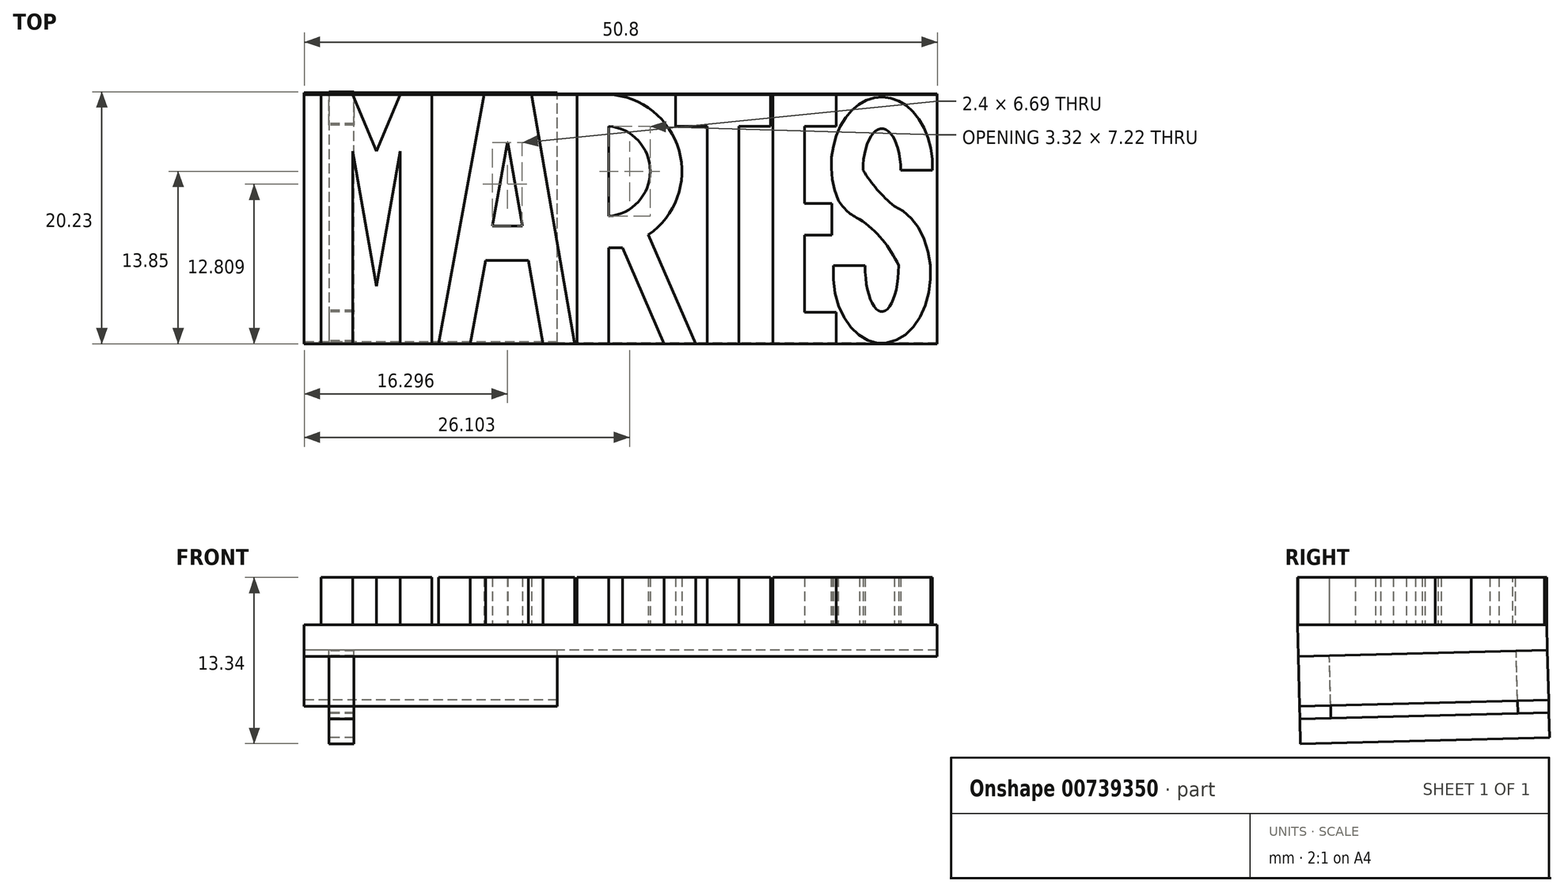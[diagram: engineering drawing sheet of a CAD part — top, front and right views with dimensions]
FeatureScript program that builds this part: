
annotation { "Feature Type Name" : "Feature", "Feature Type Description" : "" }
export const myFeature = defineFeature(function(context is Context, id is Id, definition is map)
    precondition{}
    {
        {
            var Q0;
            Q0=qCreatedBy(makeId("Front.planeOp"),FACE);
            var sketch = newSketch(context, id + "F0", { "sketchPlane" : qUnion([Q0])});
            skArc(sketch, "E0", {"start": v(21, 27.83) * mm, "mid": v(-4.5, 30.73) * mm, "end": v(-30, 27.87) * mm});
            skLineSegment(sketch, "E1", {"start": v(-30, 27.87) * mm, "end": v(-30, 32.87) * mm});
            skLineSegment(sketch, "E2", {"start": v(21, 27.83) * mm, "end": v(21, 32.87) * mm});
            skArc(sketch, "E3", {"start": v(21, 32.87) * mm, "mid": v(-4.5, 35.75) * mm, "end": v(-30, 32.87) * mm});
            skSolve(sketch);
        }
        {
            var Q0;
            Q0=makeQuery(id+"F0.imprint","IMPRINT",FACE,{"disambiguationData":[TD([[makeQuery(id+"F0.imprint","IMPRINT",EDGE,{"derivedFrom":sQuery(id+"F0.wireOp",EDGE,"E0")}),-1.0]])]});
            extrude(context, id + "F1", {"entities" : qUnion([Q0]), "depth" : 20 * mm, "offsetDistance" : 25.4 * mm});
        }
        {
            var Q0;
            Q0=makeQuery(id+"F1.opExtrude","SWEPT_FACE",FACE,{"disambiguationData":[OSD([sQuery(id+"F0.wireOp",EDGE,"E1")])]});
            var sketch = newSketch(context, id + "F2", { "sketchPlane" : qUnion([Q0])});
            skLineSegment(sketch, "E4", {"start": v(20, 32.87) * mm, "end": v(19.94, 30.33) * mm});
            skLineSegment(sketch, "E5", {"start": v(19.94, 30.33) * mm, "end": v(-0.05, 30.84) * mm});
            skLineSegment(sketch, "E6", {"start": v(-0.05, 30.84) * mm, "end": v(0, 32.87) * mm});
            skLineSegment(sketch, "E7", {"start": v(0, 32.87) * mm, "end": v(20, 32.87) * mm});
            skSolve(sketch);
        }
        {
            var Q0;
            Q0=qSketchRegion(id+"F2",true);
            extrude(context, id + "F3", {"entities" : qUnion([Q0]), "oppositeDirection" : true, "depth" : 50.8 * mm, "offsetDistance" : 25.4 * mm});
        }
        {
            var Q0;
            Q0=makeQuery(id+"F3.opExtrude","SWEPT_FACE",FACE,{"disambiguationData":[OSD([sQuery(id+"F2.wireOp",EDGE,"E5")])]});
            var sketch = newSketch(context, id + "F4", { "sketchPlane" : qUnion([Q0])});
            skLineSegment(sketch, "E8", {"start": v(-28, 19.17) * mm, "end": v(-26, 19.17) * mm});
            skLineSegment(sketch, "E9", {"start": v(-26, 19.17) * mm, "end": v(-26, 16.67) * mm});
            skLineSegment(sketch, "E10", {"start": v(-26, 16.67) * mm, "end": v(-28, 16.67) * mm});
            skLineSegment(sketch, "E11", {"start": v(-28, 16.67) * mm, "end": v(-28, 19.17) * mm});
            skLineSegment(sketch, "E12", {"start": v(-28, 1.67) * mm, "end": v(-28, -0.83) * mm});
            skLineSegment(sketch, "E13", {"start": v(-28, -0.83) * mm, "end": v(-26, -0.83) * mm});
            skLineSegment(sketch, "E14", {"start": v(-26, -0.83) * mm, "end": v(-26, 1.67) * mm});
            skLineSegment(sketch, "E15", {"start": v(-26, 1.67) * mm, "end": v(-28, 1.67) * mm});
            skLineSegment(sketch, "E16", {"start": v(-26, 1.67) * mm, "end": v(-26, 16.67) * mm});
            skLineSegment(sketch, "E17", {"start": v(-28, 1.67) * mm, "end": v(-28, 16.67) * mm});
            skSolve(sketch);
        }
        {
            var Q0;
            Q0=makeQuery(id+"F4.imprint","IMPRINT",FACE,{"disambiguationData":[TD([[makeQuery(id+"F4.imprint","IMPRINT",EDGE,{"derivedFrom":sQuery(id+"F4.wireOp",EDGE,"E8")}),1.0]])]});
            var Q1;
            Q1=makeQuery(id+"F4.imprint","IMPRINT",FACE,{"disambiguationData":[TD([[makeQuery(id+"F4.imprint","IMPRINT",EDGE,{"derivedFrom":sQuery(id+"F4.wireOp",EDGE,"E12")}),1.0]])]});
            extrude(context, id + "F5", {"entities" : qUnion([Q0, Q1]), "depth" : 5 * mm, "offsetDistance" : 25.4 * mm});
        }
        {
            var Q0;
            Q0=makeQuery(id+"F5.opExtrude","CAP_FACE",FACE,{"disambiguationData":[OSD([sQuery(id+"F4.wireOp",EDGE,"E8"),sQuery(id+"F4.wireOp",EDGE,"E9"),sQuery(id+"F4.wireOp",EDGE,"E10"),sQuery(id+"F4.wireOp",EDGE,"E11")])],"isStart":false});
            var sketch = newSketch(context, id + "F6", { "sketchPlane" : qUnion([Q0])});
            skLineSegment(sketch, "E18", {"start": v(-26, 19.17) * mm, "end": v(-26, -0.83) * mm});
            skLineSegment(sketch, "E19", {"start": v(-26, -0.83) * mm, "end": v(-28, -0.83) * mm});
            skLineSegment(sketch, "E20", {"start": v(-28, -0.83) * mm, "end": v(-28, 19.17) * mm});
            skLineSegment(sketch, "E21", {"start": v(-28, 19.17) * mm, "end": v(-26, 19.17) * mm});
            skSolve(sketch);
        }
        {
            var Q0;
            {var subQ2=sQuery(id+"F6.wireOp",EDGE,"E19");Q0=makeQuery(id+"F6.imprint","IMPRINT",FACE,{"disambiguationData":[TD([[makeQuery(id+"F6.imprint","IMPRINT",EDGE,{"derivedFrom":subQ2}),-1.0]])]});}
            var Q1;
            {var subQ0=sQuery(id+"F6.wireOp",EDGE,"E21");Q1=makeQuery(id+"F6.imprint","IMPRINT",FACE,{"disambiguationData":[TD([[makeQuery(id+"F6.imprint","IMPRINT",EDGE,{"derivedFrom":subQ0}),1.0]])]});}
            extrude(context, id + "F7", {"entities" : qUnion([Q0, Q1]), "depth" : 2 * mm, "offsetDistance" : 25.4 * mm});
        }
        {
            var Q0;
            Q0=makeQuery(id+"F3.opExtrude","SWEPT_FACE",FACE,{"disambiguationData":[OSD([sQuery(id+"F2.wireOp",EDGE,"E7")])]});
            var sketch = newSketch(context, id + "F8", { "sketchPlane" : qUnion([Q0])});
            skLineSegment(sketch, "E22", {"start": v(-28.65, 0) * mm, "end": v(-28.65, -20) * mm});
            skLineSegment(sketch, "E23", {"start": v(-28.65, -20) * mm, "end": v(-26.11, -20) * mm});
            skLineSegment(sketch, "E24", {"start": v(-26.11, -20) * mm, "end": v(-26.11, -4.55) * mm});
            skLineSegment(sketch, "E25", {"start": v(-26.11, -4.55) * mm, "end": v(-24.2, -15.36) * mm});
            skLineSegment(sketch, "E26", {"start": v(-24.2, -15.36) * mm, "end": v(-22.3, -4.55) * mm});
            skLineSegment(sketch, "E27", {"start": v(-22.3, -4.55) * mm, "end": v(-22.3, -20) * mm});
            skLineSegment(sketch, "E28", {"start": v(-22.3, -20) * mm, "end": v(-19.76, -20) * mm});
            skLineSegment(sketch, "E29", {"start": v(-19.76, -20) * mm, "end": v(-19.76, 0) * mm});
            skLineSegment(sketch, "E30", {"start": v(-19.76, 0) * mm, "end": v(-22.3, 0) * mm});
            skLineSegment(sketch, "E31", {"start": v(-22.3, 0) * mm, "end": v(-24.2, -4.55) * mm});
            skLineSegment(sketch, "E32", {"start": v(-24.2, -4.55) * mm, "end": v(-26.11, 0) * mm});
            skLineSegment(sketch, "E33", {"start": v(-26.11, 0) * mm, "end": v(-28.65, 0) * mm});
            skSolve(sketch);
        }
        {
            var Q0;
            Q0=makeQuery(id+"F8.imprint","IMPRINT",FACE,{"disambiguationData":[TD([[makeQuery(id+"F8.imprint","IMPRINT",EDGE,{"derivedFrom":sQuery(id+"F8.wireOp",EDGE,"E22")}),1.0]])]});
            extrude(context, id + "F9", {"entities" : qUnion([Q0]), "depth" : 3.8 * mm, "offsetDistance" : 25.4 * mm});
        }
        {
            var Q0;
            {var subQ1=sQuery(id+"F2.wireOp",EDGE,"E7");Q0=makeQuery(id+"F9.boolean.opBoolean","SPLIT",FACE,{"disambiguationData":[TD([makeQuery(id+"F9.opExtrude","SWEPT_FACE",FACE,{"disambiguationData":[OSD([sQuery(id+"F8.wireOp",EDGE,"E29")])]})])],"derivedFrom":makeQuery(id+"F3.opExtrude","SWEPT_FACE",FACE,{"disambiguationData":[OSD([subQ1])]})});}
            var sketch = newSketch(context, id + "F10", { "sketchPlane" : qUnion([Q0])});
            skLineSegment(sketch, "E34", {"start": v(-4.77, 0) * mm, "end": v(-4.77, -20) * mm});
            skLineSegment(sketch, "E35", {"start": v(-4.77, -20) * mm, "end": v(-2.74, -20) * mm});
            skLineSegment(sketch, "E36", {"start": v(-2.74, -20) * mm, "end": v(-2.74, 0) * mm});
            skLineSegment(sketch, "E37", {"start": v(-2.74, 0) * mm, "end": v(-4.77, 0) * mm});
            skSolve(sketch);
        }
        {
            var Q0;
            Q0=makeQuery(id+"F10.imprint","IMPRINT",FACE,{"disambiguationData":[TD([[makeQuery(id+"F10.imprint","IMPRINT",EDGE,{"derivedFrom":sQuery(id+"F10.wireOp",EDGE,"E34")}),1.0]])]});
            extrude(context, id + "F11", {"entities" : qUnion([Q0]), "depth" : 3.8 * mm, "offsetDistance" : 25.4 * mm});
        }
        {
            var Q0;
            Q0=makeQuery(id+"F3.opExtrude","SWEPT_FACE",FACE,{"disambiguationData":[OSD([sQuery(id+"F2.wireOp",EDGE,"E7")])]});
            var sketch = newSketch(context, id + "F12", { "sketchPlane" : qUnion([Q0])});
            skLineSegment(sketch, "E38", {"start": v(-1.78, 0) * mm, "end": v(0.26, 0) * mm});
            skLineSegment(sketch, "E39", {"start": v(-1.78, -20) * mm, "end": v(0.26, -20) * mm});
            skLineSegment(sketch, "E40", {"start": v(-1.78, 0) * mm, "end": v(-1.78, -20) * mm});
            skLineSegment(sketch, "E41", {"start": v(3.05, -20) * mm, "end": v(5.08, -20) * mm});
            skLineSegment(sketch, "E42", {"start": v(3.05, 0) * mm, "end": v(5.08, 0) * mm});
            skLineSegment(sketch, "E43", {"start": v(5.08, 0) * mm, "end": v(5.08, -20) * mm});
            skLineSegment(sketch, "E44", {"start": v(0.26, -20) * mm, "end": v(0.26, -8.96) * mm});
            skLineSegment(sketch, "E45", {"start": v(0.26, -8.96) * mm, "end": v(3.05, -20) * mm});
            skLineSegment(sketch, "E46", {"start": v(3.05, 0) * mm, "end": v(3.05, -10.13) * mm});
            skLineSegment(sketch, "E47", {"start": v(3.05, -10.13) * mm, "end": v(0.26, 0) * mm});
            skSolve(sketch);
        }
        {
            var Q0;
            Q0=makeQuery(id+"F12.imprint","IMPRINT",FACE,{"disambiguationData":[TD([[makeQuery(id+"F12.imprint","IMPRINT",EDGE,{"derivedFrom":sQuery(id+"F12.wireOp",EDGE,"E38")}),1.0]])]});
            extrude(context, id + "F13", {"entities" : qUnion([Q0]), "depth" : 3.8 * mm, "offsetDistance" : 25.4 * mm});
        }
        {
            var Q0;
            {var subQ1=sQuery(id+"F2.wireOp",EDGE,"E7");Q0=makeQuery(id+"F13.boolean.opBoolean","SPLIT",FACE,{"disambiguationData":[TD([makeQuery(id+"F13.opExtrude","SWEPT_FACE",FACE,{"disambiguationData":[OSD([sQuery(id+"F12.wireOp",EDGE,"E43")])]})])],"derivedFrom":makeQuery(id+"F3.opExtrude","SWEPT_FACE",FACE,{"disambiguationData":[OSD([subQ1])]})});}
            var sketch = newSketch(context, id + "F14", { "sketchPlane" : qUnion([Q0])});
            skEllipse(sketch, "E48", {"center": v(8.95, -10.06) * mm, "majorRadius": 10 * mm, "minorRadius": 3.81 * mm, "majorAxis": v(0, 1)});
            skEllipse(sketch, "E49", {"center": v(8.95, -10.06) * mm, "majorRadius": 7.97 * mm, "minorRadius": 1.78 * mm, "majorAxis": v(0, 1)});
            skLineSegment(sketch, "E50", {"start": v(10.73, -10.06) * mm, "end": v(12.76, -10.06) * mm});
            skLineSegment(sketch, "E51", {"start": v(8.95, -0.06) * mm, "end": v(8.95, -2.1) * mm});
            skLineSegment(sketch, "E52", {"start": v(8.95, -10.06) * mm, "end": v(10.73, -10.06) * mm});
            skLineSegment(sketch, "E53", {"start": v(8.95, -10.06) * mm, "end": v(8.95, -12.1) * mm});
            skLineSegment(sketch, "E54", {"start": v(8.95, -12.1) * mm, "end": v(10.67, -12.1) * mm});
            skLineSegment(sketch, "E55", {"start": v(12.54, -6.74) * mm, "end": v(10.56, -6.74) * mm});
            skLineSegment(sketch, "E56", {"start": v(8.95, -0.06) * mm, "end": v(8.95, -20.06) * mm});
            skSolve(sketch);
        }
        {
            var Q0;
            {var subQ0=sQuery(id+"F14.wireOp",EDGE,"E51");Q0=makeQuery(id+"F14.imprint","IMPRINT",FACE,{"disambiguationData":[TD([[makeQuery(id+"F14.imprint","IMPRINT",EDGE,{"derivedFrom":subQ0}),1.0]])]});}
            var Q1;
            {var subQ0=sQuery(id+"F14.wireOp",EDGE,"E50");Q1=makeQuery(id+"F14.imprint","IMPRINT",FACE,{"disambiguationData":[TD([[makeQuery(id+"F14.imprint","IMPRINT",EDGE,{"derivedFrom":subQ0}),-1.0]])]});}
            var Q2;
            {var subQ0=sQuery(id+"F14.wireOp",EDGE,"E52");Q2=makeQuery(id+"F14.imprint","IMPRINT",FACE,{"disambiguationData":[TD([[makeQuery(id+"F14.imprint","IMPRINT",EDGE,{"derivedFrom":subQ0}),-1.0]])]});}
            var Q3;
            {var subQ0=sQuery(id+"F14.wireOp",EDGE,"E56");var subQ3=sQuery(id+"F14.wireOp",EDGE,"E49");var subQ4=makeQuery(id+"F14.imprint","INTERSECT",VERTEX,{"disambiguationData":[OD(0.0)],"derivedFrom":[subQ3,subQ0]});Q3=makeQuery(id+"F14.imprint","IMPRINT",FACE,{"disambiguationData":[TD([[makeQuery(id+"F14.imprint","IMPRINT",EDGE,{"disambiguationData":[TD([[subQ4,1.0]])],"derivedFrom":subQ3}),-1.0]])]});}
            var Q4;
            {var subQ7=sQuery(id+"F14.wireOp",EDGE,"E55");Q4=makeQuery(id+"F14.imprint","IMPRINT",FACE,{"disambiguationData":[TD([[makeQuery(id+"F14.imprint","IMPRINT",EDGE,{"derivedFrom":subQ7}),-1.0]])]});}
            extrude(context, id + "F15", {"entities" : qUnion([Q0, Q1, Q2, Q3, Q4]), "depth" : 3.8 * mm, "offsetDistance" : 25.4 * mm});
        }
        {
            var Q0;
            Q0=makeQuery(id+"F3.opExtrude","SWEPT_FACE",FACE,{"disambiguationData":[OSD([sQuery(id+"F2.wireOp",EDGE,"E7")])]});
            var sketch = newSketch(context, id + "F16", { "sketchPlane" : qUnion([Q0])});
            skEllipse(sketch, "E57", {"center": v(16.77, -10) * mm, "majorRadius": 10 * mm, "minorRadius": 3.95 * mm, "majorAxis": v(0, 1)});
            skPoint(sketch, "E57.centerSnap0", {"position": v(20.8, -10) * mm});
            skEllipse(sketch, "E58", {"center": v(16.77, -10) * mm, "majorRadius": 7.5 * mm, "minorRadius": 2.22 * mm, "majorAxis": v(0, 1)});
            skSolve(sketch);
        }
        {
            var Q0;
            Q0=makeQuery(id+"F16.imprint","IMPRINT",FACE,{"disambiguationData":[TD([[makeQuery(id+"F16.imprint","IMPRINT",EDGE,{"derivedFrom":sQuery(id+"F16.wireOp",EDGE,"E58")}),-1.0]])]});
            extrude(context, id + "F17", {"entities" : qUnion([Q0]), "depth" : 3.8 * mm, "offsetDistance" : 25.4 * mm});
        }
        {
            var Q0;
            Q0=makeQuery(id+"F1.opExtrude","SWEPT_BODY",BODY,{"disambiguationData":[OSD([sQuery(id+"F0.wireOp",EDGE,"E0"),sQuery(id+"F0.wireOp",EDGE,"E1"),sQuery(id+"F0.wireOp",EDGE,"E2"),sQuery(id+"F0.wireOp",EDGE,"E3")])]});
            deleteBodies(context, id + "F18", {"entities" : qUnion([Q0])});
        }
        {
            var Q0;
            Q0=makeQuery(id+"F11.opExtrude","SWEPT_BODY",BODY,{"disambiguationData":[OSD([sQuery(id+"F10.wireOp",EDGE,"E34"),sQuery(id+"F10.wireOp",EDGE,"E35"),sQuery(id+"F10.wireOp",EDGE,"E36"),sQuery(id+"F10.wireOp",EDGE,"E37")])]});
            deleteBodies(context, id + "F19", {"entities" : qUnion([Q0])});
        }
        {
            var Q0;
            Q0=makeQuery(id+"F13.opExtrude","SWEPT_BODY",BODY,{"disambiguationData":[OSD([sQuery(id+"F12.wireOp",EDGE,"E38"),sQuery(id+"F12.wireOp",EDGE,"E39"),sQuery(id+"F12.wireOp",EDGE,"E40"),sQuery(id+"F12.wireOp",EDGE,"E41"),sQuery(id+"F12.wireOp",EDGE,"E42"),sQuery(id+"F12.wireOp",EDGE,"E43"),sQuery(id+"F12.wireOp",EDGE,"E44"),sQuery(id+"F12.wireOp",EDGE,"E45"),sQuery(id+"F12.wireOp",EDGE,"E46"),sQuery(id+"F12.wireOp",EDGE,"E47")])]});
            deleteBodies(context, id + "F20", {"entities" : qUnion([Q0])});
        }
        {
            var Q0;
            Q0=makeQuery(id+"F15.opExtrude","SWEPT_BODY",BODY,{"disambiguationData":[OSD([sQuery(id+"F0.wireOp",EDGE,"E1"),sQuery(id+"F2.wireOp",EDGE,"E4"),sQuery(id+"F2.wireOp",EDGE,"E7"),sQuery(id+"F14.wireOp",EDGE,"E48"),sQuery(id+"F14.wireOp",EDGE,"E49"),sQuery(id+"F14.wireOp",EDGE,"E50"),sQuery(id+"F14.wireOp",EDGE,"E52"),sQuery(id+"F14.wireOp",EDGE,"E54"),sQuery(id+"F14.wireOp",EDGE,"E55"),sQuery(id+"F14.wireOp",EDGE,"E56")])]});
            deleteBodies(context, id + "F21", {"entities" : qUnion([Q0])});
        }
        {
            var Q0;
            Q0=makeQuery(id+"F17.opExtrude","SWEPT_BODY",BODY,{"disambiguationData":[OSD([sQuery(id+"F16.wireOp",EDGE,"E57"),sQuery(id+"F16.wireOp",EDGE,"E58")])]});
            deleteBodies(context, id + "F22", {"entities" : qUnion([Q0])});
        }
        {
            var Q0;
            Q0=makeQuery(id+"F3.opExtrude","SWEPT_FACE",FACE,{"disambiguationData":[OSD([sQuery(id+"F2.wireOp",EDGE,"E7")])]});
            var sketch = newSketch(context, id + "F23", { "sketchPlane" : qUnion([Q0])});
            skLineSegment(sketch, "E59", {"start": v(-19.21, -20) * mm, "end": v(-16.67, -20) * mm});
            skLineSegment(sketch, "E60", {"start": v(-10.83, -20) * mm, "end": v(-8.29, -20) * mm});
            skLineSegment(sketch, "E61", {"start": v(-16.67, -20) * mm, "end": v(-15.43, -13.32) * mm});
            skLineSegment(sketch, "E62", {"start": v(-15.43, -13.32) * mm, "end": v(-12, -13.32) * mm});
            skLineSegment(sketch, "E63", {"start": v(-12, -13.32) * mm, "end": v(-10.83, -20) * mm});
            skLineSegment(sketch, "E64", {"start": v(-19.21, -20) * mm, "end": v(-15.56, 0) * mm});
            skLineSegment(sketch, "E65", {"start": v(-15.56, 0) * mm, "end": v(-11.75, 0) * mm});
            skLineSegment(sketch, "E66", {"start": v(-11.75, 0) * mm, "end": v(-8.29, -20) * mm});
            skLineSegment(sketch, "E67", {"start": v(-14.9, -10.54) * mm, "end": v(-12.5, -10.54) * mm});
            skLineSegment(sketch, "E68", {"start": v(-12.5, -10.54) * mm, "end": v(-13.66, -3.85) * mm});
            skLineSegment(sketch, "E69", {"start": v(-13.66, -3.85) * mm, "end": v(-13.68, -3.85) * mm});
            skLineSegment(sketch, "E70", {"start": v(-13.68, -3.85) * mm, "end": v(-14.9, -10.54) * mm});
            skSolve(sketch);
        }
        {
            var Q0;
            Q0=makeQuery(id+"F23.imprint","IMPRINT",FACE,{"disambiguationData":[TD([[makeQuery(id+"F23.imprint","IMPRINT",EDGE,{"derivedFrom":sQuery(id+"F23.wireOp",EDGE,"E59")}),-1.0]])]});
            extrude(context, id + "F24", {"entities" : qUnion([Q0]), "depth" : 3.8 * mm, "offsetDistance" : 25.4 * mm});
        }
        {
            var Q0;
            Q0=makeQuery(id+"F3.opExtrude","SWEPT_FACE",FACE,{"disambiguationData":[OSD([sQuery(id+"F2.wireOp",EDGE,"E7")])]});
            var sketch = newSketch(context, id + "F25", { "sketchPlane" : qUnion([Q0])});
            skLineSegment(sketch, "E71", {"start": v(-8.1, 0) * mm, "end": v(-8.1, -20) * mm});
            skLineSegment(sketch, "E72", {"start": v(-8.1, -20) * mm, "end": v(-5.56, -20) * mm});
            skLineSegment(sketch, "E73", {"start": v(-5.56, -20) * mm, "end": v(-5.56, -12.3) * mm});
            skLineSegment(sketch, "E74", {"start": v(-8.1, 0) * mm, "end": v(-5.56, 0) * mm});
            skArc(sketch, "E75", {"start": v(-2.39, -11.25) * mm, "mid": v(0.07, -4.48) * mm, "end": v(-5.56, 0) * mm});
            skLineSegment(sketch, "E76", {"start": v(-5.56, -12.3) * mm, "end": v(-4.47, -12.3) * mm});
            skLineSegment(sketch, "E77", {"start": v(-4.47, -12.3) * mm, "end": v(-1.13, -20) * mm});
            skLineSegment(sketch, "E78", {"start": v(-1.13, -20) * mm, "end": v(1.4, -20) * mm});
            skLineSegment(sketch, "E79", {"start": v(1.4, -20) * mm, "end": v(-2.39, -11.25) * mm});
            skLineSegment(sketch, "E80", {"start": v(-5.56, -2.54) * mm, "end": v(-5.56, -9.76) * mm});
            skArc(sketch, "E81", {"start": v(-5.56, -9.76) * mm, "mid": v(-2.24, -6.15) * mm, "end": v(-5.56, -2.54) * mm});
            skLineSegment(sketch, "E82", {"start": v(-2.24, -6.15) * mm, "end": v(0.3, -6.15) * mm});
            skSolve(sketch);
        }
        {
            var Q0;
            Q0 = qSketchRegion(id + "F25", true);
            extrude(context, id + "F26", {"entities" : qUnion([Q0]), "depth" : 3.8 * mm, "offsetDistance" : 25.4 * mm});
        }
        {
            var Q0;
            Q0=makeQuery(id+"F3.opExtrude","SWEPT_FACE",FACE,{"disambiguationData":[OSD([sQuery(id+"F2.wireOp",EDGE,"E7")])]});
            var sketch = newSketch(context, id + "F27", { "sketchPlane" : qUnion([Q0])});
            skLineSegment(sketch, "E83", {"start": v(-0.2, 0) * mm, "end": v(-0.2, -2.54) * mm});
            skLineSegment(sketch, "E84", {"start": v(-0.2, -2.54) * mm, "end": v(2.35, -2.54) * mm});
            skLineSegment(sketch, "E85", {"start": v(2.35, -2.54) * mm, "end": v(2.35, -20) * mm});
            skLineSegment(sketch, "E86", {"start": v(2.35, -20) * mm, "end": v(4.89, -20) * mm});
            skLineSegment(sketch, "E87", {"start": v(4.89, -20) * mm, "end": v(4.89, -2.54) * mm});
            skLineSegment(sketch, "E88", {"start": v(4.89, -2.54) * mm, "end": v(7.43, -2.54) * mm});
            skLineSegment(sketch, "E89", {"start": v(7.43, -2.54) * mm, "end": v(7.43, 0) * mm});
            skLineSegment(sketch, "E90", {"start": v(7.43, 0) * mm, "end": v(-0.2, 0) * mm});
            skSolve(sketch);
        }
        {
            var Q0;
            Q0 = qSketchRegion(id + "F27", true);
            extrude(context, id + "F28", {"entities" : qUnion([Q0]), "depth" : 3.8 * mm, "offsetDistance" : 25.4 * mm});
        }
        {
            var Q0;
            Q0=makeQuery(id+"F3.opExtrude","SWEPT_FACE",FACE,{"disambiguationData":[OSD([sQuery(id+"F2.wireOp",EDGE,"E7")])]});
            var sketch = newSketch(context, id + "F29", { "sketchPlane" : qUnion([Q0])});
            skLineSegment(sketch, "E91", {"start": v(7.62, 0) * mm, "end": v(7.62, -20) * mm});
            skLineSegment(sketch, "E92", {"start": v(7.62, -20) * mm, "end": v(12.7, -20) * mm});
            skLineSegment(sketch, "E93", {"start": v(12.7, -20) * mm, "end": v(12.7, -17.46) * mm});
            skLineSegment(sketch, "E94", {"start": v(12.7, -17.46) * mm, "end": v(10.16, -17.46) * mm});
            skLineSegment(sketch, "E95", {"start": v(10.16, -17.46) * mm, "end": v(10.16, -11.27) * mm});
            skLineSegment(sketch, "E96", {"start": v(10.16, -11.27) * mm, "end": v(12.35, -11.27) * mm});
            skLineSegment(sketch, "E97", {"start": v(12.35, -11.27) * mm, "end": v(12.35, -8.73) * mm});
            skLineSegment(sketch, "E98", {"start": v(12.35, -8.73) * mm, "end": v(10.16, -8.73) * mm});
            skLineSegment(sketch, "E99", {"start": v(10.16, -8.73) * mm, "end": v(10.16, -2.54) * mm});
            skLineSegment(sketch, "E100", {"start": v(10.16, -2.54) * mm, "end": v(12.7, -2.54) * mm});
            skLineSegment(sketch, "E101", {"start": v(12.7, -2.54) * mm, "end": v(12.7, 0) * mm});
            skLineSegment(sketch, "E102", {"start": v(12.7, 0) * mm, "end": v(7.62, 0) * mm});
            skSolve(sketch);
        }
        {
            var Q0;
            Q0 = qSketchRegion(id + "F29", true);
            extrude(context, id + "F30", {"entities" : qUnion([Q0]), "depth" : 3.8 * mm, "offsetDistance" : 25.4 * mm});
        }
        {
            var Q0;
            Q0=makeQuery(id+"F3.opExtrude","SWEPT_FACE",FACE,{"disambiguationData":[OSD([sQuery(id+"F2.wireOp",EDGE,"E7")])]});
            var sketch = newSketch(context, id + "F31", { "sketchPlane" : qUnion([Q0])});
            skEllipse(sketch, "E103", {"center": v(16.35, -5.7) * mm, "majorRadius": 5.5 * mm, "minorRadius": 4.06 * mm, "majorAxis": v(0, -1)});
            skEllipse(sketch, "E104", {"center": v(16.35, -6.07) * mm, "majorRadius": 3.34 * mm, "minorRadius": 1.51 * mm, "majorAxis": v(0, 1)});
            skLineSegment(sketch, "E105", {"start": v(16.35, -0.2) * mm, "end": v(16.35, -2.73) * mm});
            skLineSegment(sketch, "E106", {"start": v(14.84, -6.07) * mm, "end": v(12.3, -6.07) * mm});
            skLineSegment(sketch, "E107", {"start": v(17.86, -6.07) * mm, "end": v(20.4, -6.07) * mm});
            skEllipse(sketch, "E108", {"center": v(16.35, -14.37) * mm, "majorRadius": 5.59 * mm, "minorRadius": 3.91 * mm, "majorAxis": v(0, 1)});
            skEllipse(sketch, "E109", {"center": v(16.35, -13.73) * mm, "majorRadius": 3.68 * mm, "minorRadius": 1.35 * mm, "majorAxis": v(0, -1)});
            skLineSegment(sketch, "E110", {"start": v(16.35, -17.42) * mm, "end": v(16.35, -19.96) * mm});
            skLineSegment(sketch, "E111", {"start": v(15, -13.73) * mm, "end": v(12.46, -13.73) * mm});
            skLineSegment(sketch, "E112", {"start": v(17.7, -13.73) * mm, "end": v(20.24, -13.73) * mm});
            skArc(sketch, "E113", {"start": v(14.84, -6.07) * mm, "mid": v(16.58, -8.27) * mm, "end": v(18.8, -10) * mm});
            skPoint(sketch, "E113.endSnap0", {"position": v(20.8, -10) * mm});
            skArc(sketch, "E114", {"start": v(20.24, -13.73) * mm, "mid": v(19.99, -11.68) * mm, "end": v(18.8, -10) * mm});
            skArc(sketch, "E115", {"start": v(12.3, -6.07) * mm, "mid": v(12.8, -8.4) * mm, "end": v(14.56, -10) * mm});
            skArc(sketch, "E116", {"start": v(17.7, -13.73) * mm, "mid": v(16.4, -11.65) * mm, "end": v(14.56, -10) * mm});
            skLineSegment(sketch, "E117", {"start": v(15.55, -10.77) * mm, "end": v(17.2, -8.84) * mm});
            skSolve(sketch);
        }
        {
            var Q0;
            {var subQ0=sQuery(id+"F31.wireOp",EDGE,"E105");Q0=makeQuery(id+"F31.imprint","IMPRINT",FACE,{"disambiguationData":[TD([[makeQuery(id+"F31.imprint","IMPRINT",EDGE,{"derivedFrom":subQ0}),1.0]])]});}
            var Q1;
            {var subQ0=sQuery(id+"F31.wireOp",EDGE,"E105");Q1=makeQuery(id+"F31.imprint","IMPRINT",FACE,{"disambiguationData":[TD([[makeQuery(id+"F31.imprint","IMPRINT",EDGE,{"derivedFrom":subQ0}),-1.0]])]});}
            var Q2;
            {var subQ0=sQuery(id+"F31.wireOp",EDGE,"E106");Q2=makeQuery(id+"F31.imprint","IMPRINT",FACE,{"disambiguationData":[TD([[makeQuery(id+"F31.imprint","IMPRINT",EDGE,{"derivedFrom":subQ0}),1.0]])]});}
            var Q3;
            {var subQ5=sQuery(id+"F31.wireOp",EDGE,"E112");Q3=makeQuery(id+"F31.imprint","IMPRINT",FACE,{"disambiguationData":[TD([[makeQuery(id+"F31.imprint","IMPRINT",EDGE,{"derivedFrom":subQ5}),1.0]])]});}
            var Q4;
            {var subQ0=sQuery(id+"F31.wireOp",EDGE,"E110");Q4=makeQuery(id+"F31.imprint","IMPRINT",FACE,{"disambiguationData":[TD([[makeQuery(id+"F31.imprint","IMPRINT",EDGE,{"derivedFrom":subQ0}),1.0]])]});}
            var Q5;
            {var subQ0=sQuery(id+"F31.wireOp",EDGE,"E110");Q5=makeQuery(id+"F31.imprint","IMPRINT",FACE,{"disambiguationData":[TD([[makeQuery(id+"F31.imprint","IMPRINT",EDGE,{"derivedFrom":subQ0}),-1.0]])]});}
            var Q6;
            {var subQ0=sQuery(id+"F31.wireOp",EDGE,"E109");var subQ1=sQuery(id+"F31.wireOp",EDGE,"E103");var subQ2=makeQuery(id+"F31.imprint","INTERSECT",VERTEX,{"disambiguationData":[OD(0.0)],"derivedFrom":[subQ1,subQ0]});Q6=makeQuery(id+"F31.imprint","IMPRINT",FACE,{"disambiguationData":[TD([[makeQuery(id+"F31.imprint","IMPRINT",EDGE,{"disambiguationData":[TD([[subQ2,1.0]])],"derivedFrom":subQ1}),1.0]])]});}
            var Q7;
            {var subQ0=sQuery(id+"F31.wireOp",EDGE,"E109");var subQ1=sQuery(id+"F31.wireOp",EDGE,"E103");var subQ2=makeQuery(id+"F31.imprint","INTERSECT",VERTEX,{"disambiguationData":[OD(0.0)],"derivedFrom":[subQ1,subQ0]});Q7=makeQuery(id+"F31.imprint","IMPRINT",FACE,{"disambiguationData":[TD([[makeQuery(id+"F31.imprint","IMPRINT",EDGE,{"disambiguationData":[TD([[subQ2,1.0]])],"derivedFrom":subQ1}),-1.0]])]});}
            var Q8;
            {var subQ1=sQuery(id+"F31.wireOp",EDGE,"E104");var subQ3=sQuery(id+"F31.wireOp",EDGE,"E108");var subQ4=makeQuery(id+"F31.imprint","INTERSECT",VERTEX,{"disambiguationData":[OD(0.0)],"derivedFrom":[subQ1,subQ3]});Q8=makeQuery(id+"F31.imprint","IMPRINT",FACE,{"disambiguationData":[TD([[makeQuery(id+"F31.imprint","IMPRINT",EDGE,{"disambiguationData":[TD([[subQ4,1.0]])],"derivedFrom":subQ3}),-1.0]])]});}
            var Q9;
            {var subQ0=sQuery(id+"F31.wireOp",EDGE,"E108");var subQ1=sQuery(id+"F31.wireOp",EDGE,"E104");var subQ2=makeQuery(id+"F31.imprint","INTERSECT",VERTEX,{"disambiguationData":[OD(0.0)],"derivedFrom":[subQ1,subQ0]});Q9=makeQuery(id+"F31.imprint","IMPRINT",FACE,{"disambiguationData":[TD([[makeQuery(id+"F31.imprint","IMPRINT",EDGE,{"disambiguationData":[TD([[subQ2,-1.0]])],"derivedFrom":subQ1}),1.0]])]});}
            var Q10;
            {var subQ3=sQuery(id+"F31.wireOp",EDGE,"E108");var subQ9=sQuery(id+"F31.wireOp",EDGE,"E104");var subQ10=makeQuery(id+"F31.imprint","INTERSECT",VERTEX,{"disambiguationData":[OD(0.0)],"derivedFrom":[subQ9,subQ3]});Q10=makeQuery(id+"F31.imprint","IMPRINT",FACE,{"disambiguationData":[TD([[makeQuery(id+"F31.imprint","IMPRINT",EDGE,{"disambiguationData":[TD([[subQ10,-1.0]])],"derivedFrom":subQ9}),-1.0]])]});}
            var Q11;
            {var subQ0=sQuery(id+"F31.wireOp",EDGE,"E117");var subQ1=sQuery(id+"F31.wireOp",EDGE,"E109");var subQ3=makeQuery(id+"F31.imprint","INTERSECT",VERTEX,{"derivedFrom":[subQ1,subQ0]});Q11=makeQuery(id+"F31.imprint","IMPRINT",FACE,{"disambiguationData":[TD([[makeQuery(id+"F31.imprint","IMPRINT",EDGE,{"disambiguationData":[TD([[subQ3,-1.0]])],"derivedFrom":subQ1}),1.0]])]});}
            var Q12;
            {var subQ0=sQuery(id+"F31.wireOp",EDGE,"E113");var subQ1=sQuery(id+"F31.wireOp",EDGE,"E108");var subQ3=makeQuery(id+"F31.imprint","INTERSECT",VERTEX,{"derivedFrom":[subQ1,subQ0]});Q12=makeQuery(id+"F31.imprint","IMPRINT",FACE,{"disambiguationData":[TD([[makeQuery(id+"F31.imprint","IMPRINT",EDGE,{"disambiguationData":[TD([[subQ3,1.0]])],"derivedFrom":subQ1}),1.0]])]});}
            var Q13;
            {var subQ0=sQuery(id+"F31.wireOp",EDGE,"E108");var subQ6=sQuery(id+"F31.wireOp",EDGE,"E103");var subQ7=makeQuery(id+"F31.imprint","INTERSECT",VERTEX,{"disambiguationData":[OD(0.0)],"derivedFrom":[subQ6,subQ0]});Q13=makeQuery(id+"F31.imprint","IMPRINT",FACE,{"disambiguationData":[TD([[makeQuery(id+"F31.imprint","IMPRINT",EDGE,{"disambiguationData":[TD([[subQ7,1.0]])],"derivedFrom":subQ6}),1.0]])]});}
            var Q14;
            {var subQ0=sQuery(id+"F31.wireOp",EDGE,"E117");var subQ1=sQuery(id+"F31.wireOp",EDGE,"E104");var subQ2=makeQuery(id+"F31.imprint","INTERSECT",VERTEX,{"derivedFrom":[subQ1,subQ0]});Q14=makeQuery(id+"F31.imprint","IMPRINT",FACE,{"disambiguationData":[TD([[makeQuery(id+"F31.imprint","IMPRINT",EDGE,{"disambiguationData":[TD([[subQ2,-1.0]])],"derivedFrom":subQ1}),1.0]])]});}
            var Q15;
            {var subQ1=sQuery(id+"F31.wireOp",EDGE,"E104");var subQ3=sQuery(id+"F31.wireOp",EDGE,"E108");var subQ4=makeQuery(id+"F31.imprint","INTERSECT",VERTEX,{"disambiguationData":[OD(1.0)],"derivedFrom":[subQ1,subQ3]});Q15=makeQuery(id+"F31.imprint","IMPRINT",FACE,{"disambiguationData":[TD([[makeQuery(id+"F31.imprint","IMPRINT",EDGE,{"disambiguationData":[TD([[subQ4,1.0]])],"derivedFrom":subQ3}),-1.0]])]});}
            var Q16;
            {var subQ1=sQuery(id+"F31.wireOp",EDGE,"E104");var subQ3=sQuery(id+"F31.wireOp",EDGE,"E108");var subQ4=makeQuery(id+"F31.imprint","INTERSECT",VERTEX,{"disambiguationData":[OD(1.0)],"derivedFrom":[subQ1,subQ3]});Q16=makeQuery(id+"F31.imprint","IMPRINT",FACE,{"disambiguationData":[TD([[makeQuery(id+"F31.imprint","IMPRINT",EDGE,{"disambiguationData":[TD([[subQ4,-1.0]])],"derivedFrom":subQ3}),-1.0]])]});}
            extrude(context, id + "F32", {"entities" : qUnion([Q0, Q1, Q2, Q3, Q4, Q5, Q6, Q7, Q8, Q9, Q10, Q11, Q12, Q13, Q14, Q15, Q16]), "depth" : 3.8 * mm, "offsetDistance" : 25.4 * mm});
        }
        {
            var Q0;
            Q0=makeQuery(id+"F3.opExtrude","SWEPT_FACE",FACE,{"disambiguationData":[OSD([sQuery(id+"F2.wireOp",EDGE,"E5")])]});
            var sketch = newSketch(context, id + "F33", { "sketchPlane" : qUnion([Q0])});
            skLineSegment(sketch, "E118.bottom", {"start": v(-30, 19.17) * mm, "end": v(-9.68, 19.17) * mm});
            skLineSegment(sketch, "E118.top", {"start": v(-30, -0.83) * mm, "end": v(-9.68, -0.83) * mm});
            skLineSegment(sketch, "E118.left", {"start": v(-30, 19.17) * mm, "end": v(-30, -0.83) * mm});
            skLineSegment(sketch, "E118.right", {"start": v(-9.68, 19.17) * mm, "end": v(-9.68, -0.83) * mm});
            skSolve(sketch);
        }
        {
            var Q0;
            Q0=makeQuery(id+"F33.imprint","IMPRINT",FACE,{"disambiguationData":[TD([[makeQuery(id+"F33.imprint","IMPRINT",EDGE,{"derivedFrom":sQuery(id+"F33.wireOp",EDGE,"E118.bottom")}),1.0]])]});
            extrude(context, id + "F34", {"entities" : qUnion([Q0]), "depth" : 4 * mm, "offsetDistance" : 25.4 * mm});
        }
    });
